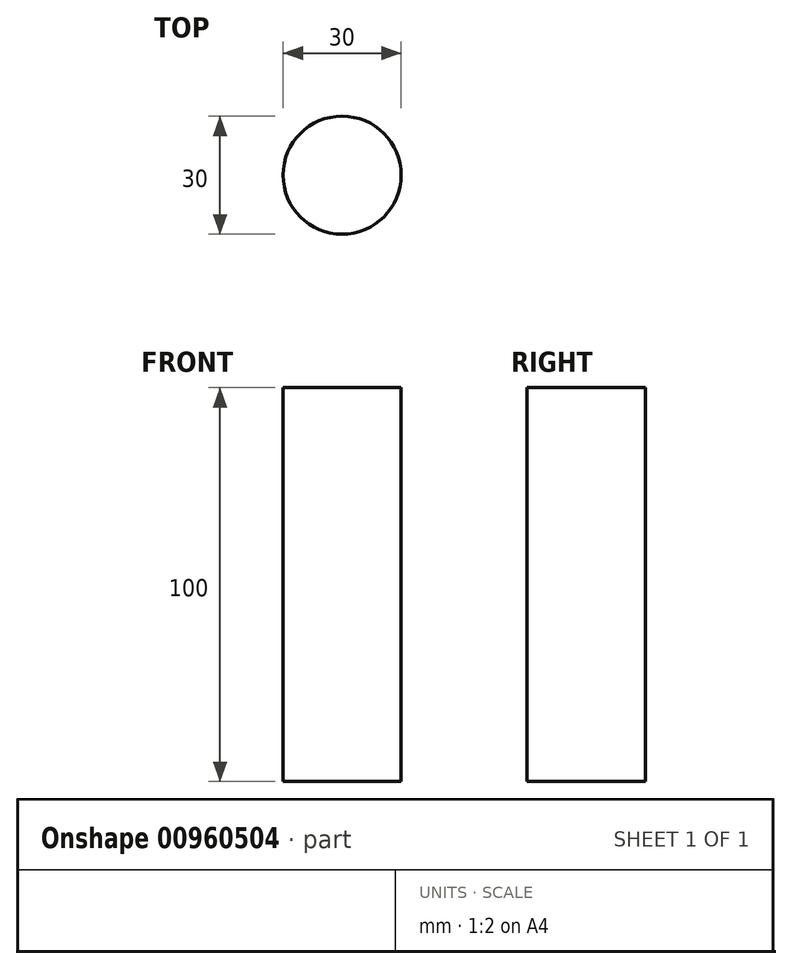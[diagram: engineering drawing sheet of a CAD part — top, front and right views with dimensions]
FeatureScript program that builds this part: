
annotation { "Feature Type Name" : "Feature", "Feature Type Description" : "" }
export const myFeature = defineFeature(function(context is Context, id is Id, definition is map)
    precondition{}
    {
        {
            var Q0;
            Q0=qCreatedBy(makeId("Top.planeOp"),FACE);
            var sketch = newSketch(context, id + "F0", { "sketchPlane" : qUnion([Q0])});
            skCircle(sketch, "E0", {"center": v(0, 0) * mm, "radius": 15 * mm});
            skSolve(sketch);
        }
        {
            var Q0;
            Q0 = qSketchRegion(id + "F0", true);
            extrude(context, id + "F1", {"entities" : qUnion([Q0]), "endBound" : BoundingType.SYMMETRIC, "depth" : 100 * mm, "offsetDistance" : 25 * mm});
        }
    });
